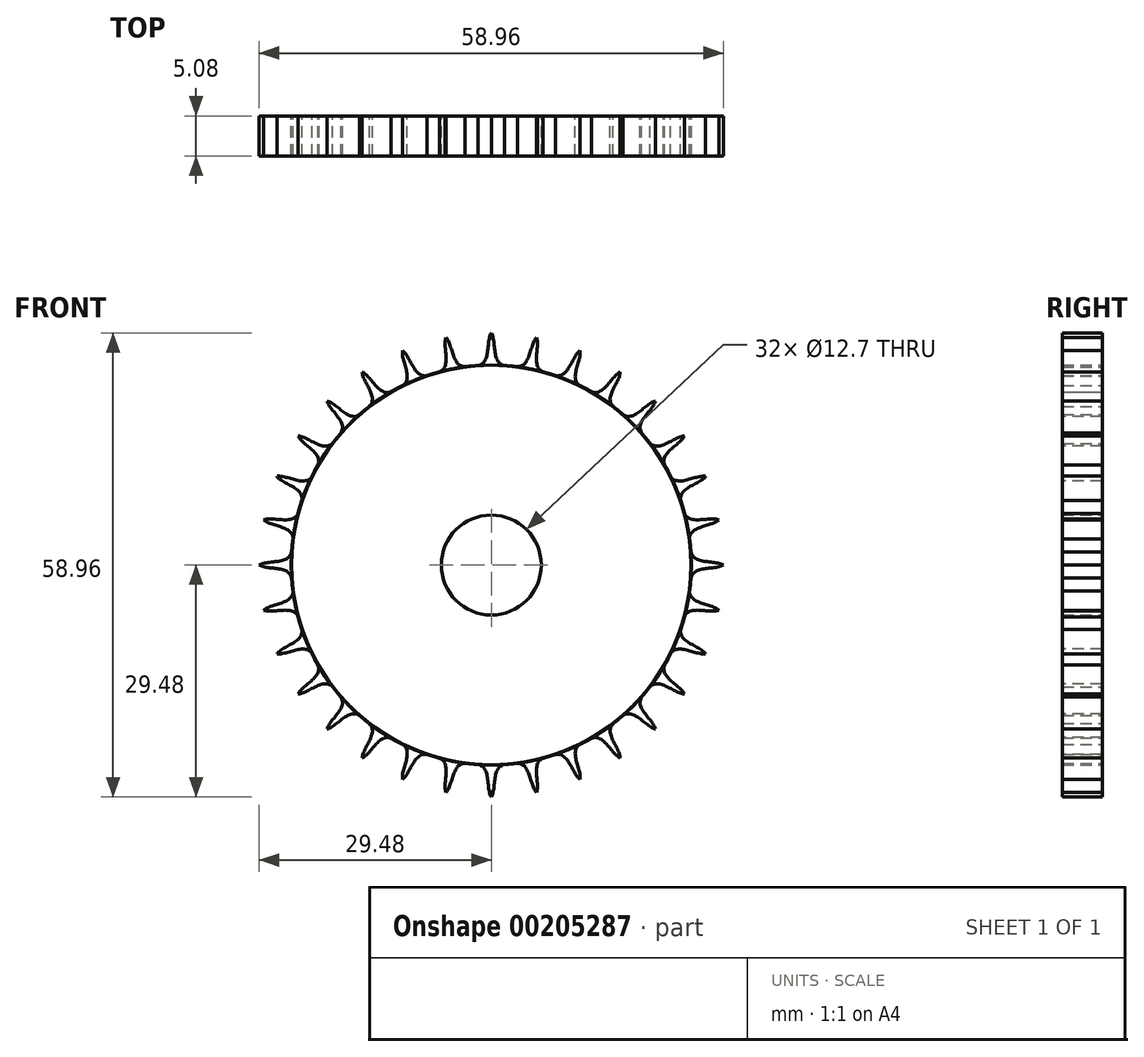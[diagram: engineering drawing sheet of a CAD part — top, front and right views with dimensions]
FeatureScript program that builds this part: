
annotation { "Feature Type Name" : "Feature", "Feature Type Description" : "" }
export const myFeature = defineFeature(function(context is Context, id is Id, definition is map)
    precondition{}
    {
        {
            var Q0;
            Q0=qCreatedBy(makeId("Front.planeOp"),FACE);
            var sketch = newSketch(context, id + "F0", { "sketchPlane" : qUnion([Q0])});
            skCircle(sketch, "E0", {"center": v(0, 0) * mm, "radius": 6.35 * mm});
            skFitSpline(sketch, "E1", {"points": [v(-1.66, 25.35) * mm, v(0, 29.48) * mm], "startDerivative": vector(4.97, 1.17) * mm, "endDerivative": vector(2.05, 3.48) * mm});
            skFitSpline(sketch, "E2.MirrorCS", {"points": [v(1.66, 25.35) * mm, v(0, 29.48) * mm], "startDerivative": vector(-4.97, 1.17) * mm, "endDerivative": vector(-2.05, 3.48) * mm});
            skArc(sketch, "E3", {"start": v(1.66, 25.35) * mm, "mid": v(0, 25.47) * mm, "end": v(-1.66, 25.35) * mm});
            skCircle(sketch, "E4", {"center": v(0, 0) * mm, "radius": 25.4 * mm});
            skSolve(sketch);
        }
        {
            var Q0;
            Q0 = qSketchRegion(id + "F0", true);
            extrude(context, id + "F1", {"entities" : qUnion([Q0]), "endBound" : BoundingType.SYMMETRIC, "depth" : 5.08 * mm});
        }
        {
            var Q0;
            Q0=makeQuery(id+"F1.opExtrude","SWEPT_BODY",BODY,{"disambiguationData":[OSD([sQuery(id+"F0.wireOp",EDGE,"E1"),sQuery(id+"F0.wireOp",EDGE,"E2.MirrorCS"),sQuery(id+"F0.wireOp",EDGE,"E3")])]});
            var Q1;
            Q1=sQuery(id+"F0.wireOp",EDGE,"E0");
            circularPattern(context, id + "F2", {"entities" : qUnion([Q0]), "axis" : qUnion([Q1]), "angle" : 360 * degree, "instanceCount" : 32, "equalSpace" : true});
        }
    });
